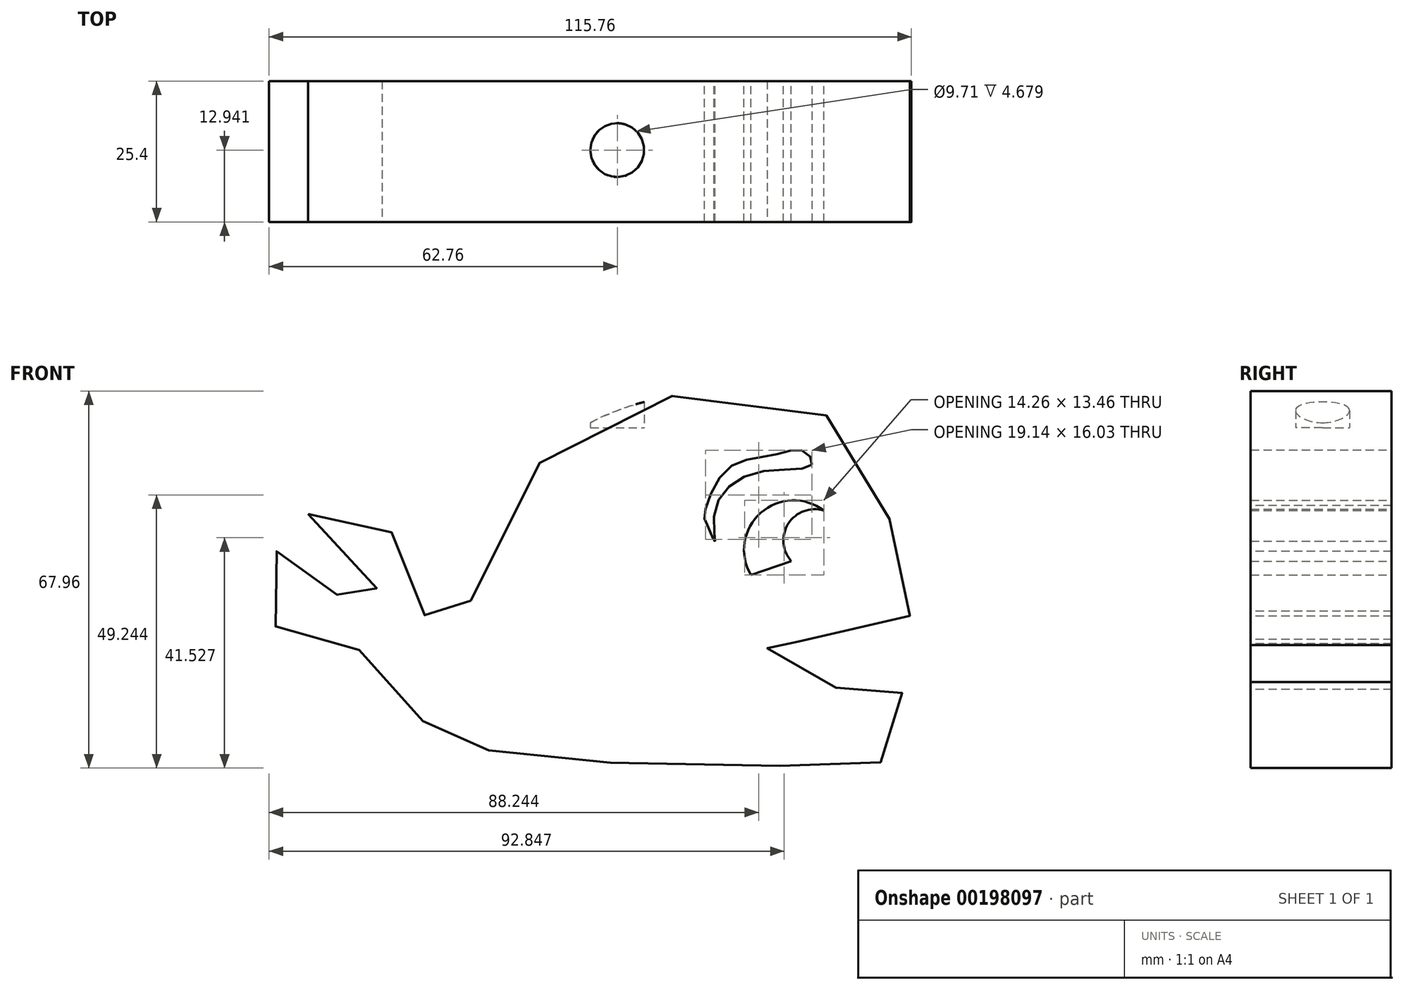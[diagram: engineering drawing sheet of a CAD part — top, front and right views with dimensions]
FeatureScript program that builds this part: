
annotation { "Feature Type Name" : "Feature", "Feature Type Description" : "" }
export const myFeature = defineFeature(function(context is Context, id is Id, definition is map)
    precondition{}
    {
        {
            var Q0;
            Q0=qCreatedBy(makeId("Front.planeOp"),FACE);
            var sketch = newSketch(context, id + "F0", { "sketchPlane" : qUnion([Q0])});
            skFitSpline(sketch, "E0", {"points": [v(-59.23, 22.58) * mm, v(-48.8, 23.04) * mm, v(-41.05, 12.74) * mm, v(-37.92, 3.59) * mm, v(-34.2, 0) * mm, v(-24.26, 21.19) * mm, v(-4.46, 40.87) * mm, v(31.09, 42.03) * mm, v(44.4, 25.59) * mm, v(48.11, 9.38) * mm, v(47.76, 1.62) * mm, v(25.88, 1.16) * mm, v(24.84, 4.17) * mm, v(24.03, -5.67) * mm, v(34.56, -8.92) * mm, v(40.82, -7.87) * mm, v(47.53, -9.38) * mm, v(48.57, -18.87) * mm, v(39.54, -23.04) * mm, v(23.22, -22.7) * mm, v(-16.04, -21.77) * mm, v(-28.28, -19.59) * mm, v(-34.17, -17.28) * mm, v(-42.31, -11.36) * mm, v(-50.89, -1.5) * mm, v(-63.16, 0) * mm, v(-66.29, 9.96) * mm, v(-65.13, 15.86) * mm, v(-60.85, 12.04) * mm, v(-52.74, 7.4) * mm, v(-46.26, 5.2) * mm, v(-49.73, 13.2) * mm, v(-59.23, 22.58) * mm]});
            skLineSegment(sketch, "E1", {"start": v(20.55, 11.58) * mm, "end": v(37.11, 17.25) * mm});
            skArc(sketch, "E2", {"start": v(37.11, 17.25) * mm, "mid": v(25.36, 24.56) * mm, "end": v(20.55, 11.58) * mm});
            skArc(sketch, "E3", {"start": v(33.68, 23.2) * mm, "mid": v(27.3, 20.85) * mm, "end": v(27.83, 14.07) * mm});
            skFitSpline(sketch, "E4", {"points": [v(31.53, 31.47) * mm, v(30.14, 33.9) * mm, v(24.58, 33.2) * mm, v(16.24, 30.66) * mm, v(12.19, 22.32) * mm, v(12.65, 20.7) * mm, v(14.04, 17.69) * mm, v(14.04, 23.01) * mm, v(21.68, 30.08) * mm, v(31.53, 31.47) * mm]});
            skLineSegment(sketch, "E5", {"start": v(-2.72, 36.7) * mm, "end": v(-2.72, 36.7) * mm});
            skSolve(sketch);
        }
        {
            var Q0;
            Q0=makeQuery(id+"F0.imprint","IMPRINT",FACE,{"disambiguationData":[TD([[makeQuery(id+"F0.imprint","IMPRINT",EDGE,{"derivedFrom":sQuery(id+"F0.wireOp",EDGE,"E0")}),-1.0]])]});
            var Q1;
            {var subQ3=sQuery(id+"F0.wireOp",EDGE,"E3");Q1=makeQuery(id+"F0.imprint","IMPRINT",FACE,{"disambiguationData":[TD([[makeQuery(id+"F0.imprint","IMPRINT",EDGE,{"derivedFrom":subQ3}),1.0]])]});}
            extrude(context, id + "F1", {"entities" : qUnion([Q0, Q1]), "depth" : 25.4 * mm});
        }
        {
            var Q0;
            Q0=qCreatedBy(makeId("Top.planeOp"),FACE);
            cPlane(context, id + "F2", {"entities" : qUnion([Q0]), "cplaneType" : CPlaneType.OFFSET, "offset" : 38.1 * mm, "width" : 152.4 * mm, "height" : 152.4 * mm});
        }
        {
            var Q0;
            Q0=qCreatedBy(id+"F2.planeOp",FACE);
            var sketch = newSketch(context, id + "F3", { "sketchPlane" : qUnion([Q0])});
            skCircle(sketch, "E6", {"center": v(-3.53, -12.46) * mm, "radius": 4.85 * mm});
            skSolve(sketch);
        }
        {
            var Q0;
            Q0 = qSketchRegion(id + "F3", true);
            extrude(context, id + "F4", {"entities" : qUnion([Q0]), "operationType" : NewBodyOperationType.REMOVE, "depth" : 57.9 * mm});
        }
    });
